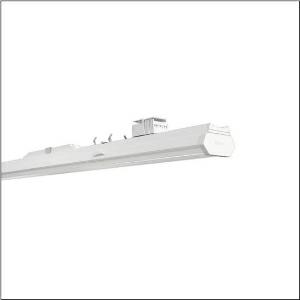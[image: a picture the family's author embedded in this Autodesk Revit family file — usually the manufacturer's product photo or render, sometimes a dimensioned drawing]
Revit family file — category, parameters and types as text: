
# Revit family: licross_21_protected_ho_52tp13mn4fxs
name_source: partatom
category: Lighting Fixtures
units: mm (PartAtom-declared; Revit-internal decimal feet)

## family parameters
Cut with Voids When Loaded = No
Host = Face
Light Source = No
Part Type = Normal
Room Calculation Point = No
Round Connector Dimension = Use Diameter
Shared = No

## types (1)
- --- (1 x LED, 15060 lm, 83.2 W, 4000K)
    Apparent Load = 83 VA
    CIE Flux Codes = 89 96 99 100 99
    Color Rendering = 80
    Color Temperature = 4000K
    Default Elevation = 1800 mm
    Description = Licross 21 Protected HO, luminaire insert, of sheet steel, galvanised, coil coated, white, length: 1.500mm, width: 66mm, height: 67mm, LED rated luminous flux: 15.060lm, light colour: 840, SDCM (Standard Deviation of Colour Matching)MacAdam ≤ 3 SDCM (initial), control gear: ON/OFF Multilumen, with plug, 3-pole, with phase selection, mains connection: 220..240V, AC, 50/60Hz, rated input power: 83W, internal wiring halogen-free, primary light control with lens, of plastic, primary optical cover: cover, of PMMA, light emission: direct distribution, primary light characteristic: symmetric, protection rating (complete): IP64, insulation class (complete): insulation class I (protective earthing), certification: CE, ENEC, VDE, UKCA, protection symbol: D if used in an environment with conductive dust loads with corresponding accessories, impact resistance: IK06, permissible ambient temperature for indoor applications: -35..+35°C, corresponds to IFS (International Featured Standards) requirements for safety and quality in the food industry, reducing of maximum allowable ambient temperature of 5°C with ceiling mounting, LABS conformity tested according to VDMA 24364:2018-05, The light source and the operating device comply with the requirements of the Ecodesign Regulation (EU) 2019/2020 and are replaceable in accordance with this regulation, packaging unit: 1 piece
    Height = 92 mm
    Lamp = 1 x LED
    Lamp Light Flux = 15060 lm
    Lamp Power = 83.2 W
    Lamp count = 1
    Length = 1500 mm
    Luminous efficacy = 181 lm/W
    Manufacturer = Siteco
    ModVariant = No
    Model = 52TP13MN4FXS
    Mounting Place = Ceiling
    Mounting Type = Pendant
    Number of Poles = 1
    OnlyDefault = Yes
    Power Factor = 1
    Product Name = Licross 21 Protected HO
    Product group = luminaire insert | ceiling pendant
    ProductGroupID = 901
    Protection Class = Protection class I
    Protection Degree = IP 64
    RLX_Detail_Level = 1
    RLX_Emergency_Light_Flux = 0 lm
    RLX_Emergency_Type = 0
    RLX_Emergency_Type_DB = No
    RlxData = <blob elided: 22137 chars, md5=8760e0a8>
    Socket = socket
    Standby Power = 0 W
    System Light Flux = 15060 lm
    System Power = 83 W
    Type Comments = factory setting: luminous flux: 100 % | (A | C | E) | 195 mA
    Type Image = l_1256148.jpg
    URL = http://relux.com
    VarID = @adj_108975
    Voltage = 0 V
    Weight = 0.00 kg
    Width = 88 mm

## geometry (parser evidence)
native form markers: Blend x4, Sweep x11
no freeform markers — native parametric forms only
